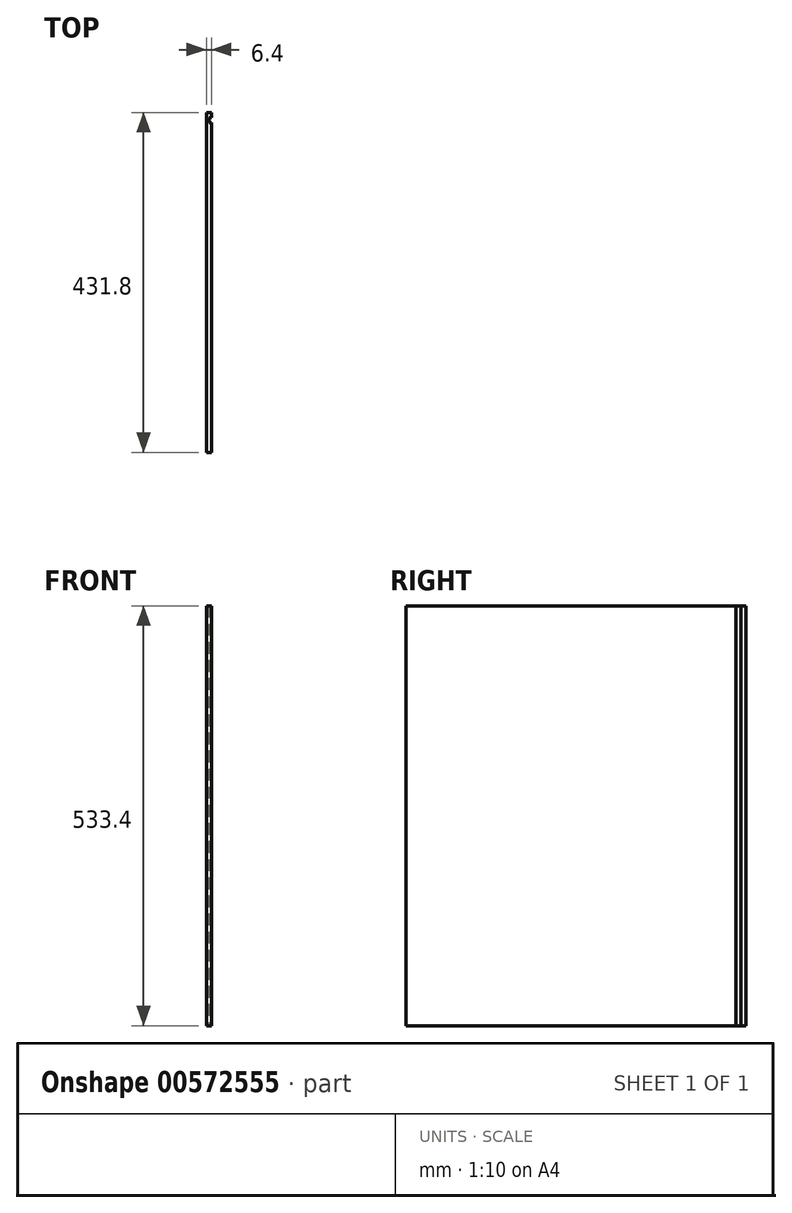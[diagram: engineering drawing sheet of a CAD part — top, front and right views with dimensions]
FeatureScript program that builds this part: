
annotation { "Feature Type Name" : "Feature", "Feature Type Description" : "" }
export const myFeature = defineFeature(function(context is Context, id is Id, definition is map)
    precondition{}
    {
        {
            var Q0;
            Q0=qCreatedBy(makeId("Right.planeOp"),FACE);
            var sketch = newSketch(context, id + "F0", { "sketchPlane" : qUnion([Q0])});
            skLineSegment(sketch, "E0.bottom", {"start": v(-326.3, 269.4) * mm, "end": v(105.5, 269.4) * mm});
            skLineSegment(sketch, "E0.top", {"start": v(-326.3, -264) * mm, "end": v(105.5, -264) * mm});
            skLineSegment(sketch, "E0.left", {"start": v(-326.3, 269.4) * mm, "end": v(-326.3, -264) * mm});
            skLineSegment(sketch, "E0.right", {"start": v(105.5, 269.4) * mm, "end": v(105.5, -264) * mm});
            skLineSegment(sketch, "E1.bottom", {"start": v(99.15, 279.55) * mm, "end": v(92.8, 279.55) * mm});
            skLineSegment(sketch, "E1.top", {"start": v(99.15, -274.17) * mm, "end": v(92.8, -274.17) * mm});
            skLineSegment(sketch, "E1.left", {"start": v(99.15, 279.55) * mm, "end": v(99.15, -274.17) * mm});
            skLineSegment(sketch, "E1.right", {"start": v(92.8, 279.55) * mm, "end": v(92.8, -274.17) * mm});
            skSolve(sketch);
        }
        {
            var Q0;
            {var subQ0=sQuery(id+"F0.wireOp",EDGE,"E0.left");Q0=makeQuery(id+"F0.imprint","IMPRINT",FACE,{"disambiguationData":[TD([[makeQuery(id+"F0.imprint","IMPRINT",EDGE,{"derivedFrom":subQ0}),1.0]])]});}
            var Q1;
            {var subQ0=sQuery(id+"F0.wireOp",EDGE,"E0.right");Q1=makeQuery(id+"F0.imprint","IMPRINT",FACE,{"disambiguationData":[TD([[makeQuery(id+"F0.imprint","IMPRINT",EDGE,{"derivedFrom":subQ0}),-1.0]])]});}
            var Q2;
            {var subQ0=sQuery(id+"F0.wireOp",EDGE,"E1.right");var subQ1=sQuery(id+"F0.wireOp",EDGE,"E0.bottom");var subQ2=makeQuery(id+"F0.imprint","INTERSECT",VERTEX,{"derivedFrom":[subQ1,subQ0]});Q2=makeQuery(id+"F0.imprint","IMPRINT",FACE,{"disambiguationData":[TD([[makeQuery(id+"F0.imprint","IMPRINT",EDGE,{"disambiguationData":[TD([[subQ2,-1.0]])],"derivedFrom":subQ1}),-1.0]])]});}
            extrude(context, id + "F1", {"entities" : qUnion([Q0, Q1, Q2]), "oppositeDirection" : true, "depth" : 3.2 * mm, "offsetDistance" : 25.4 * mm});
        }
        {
            var Q0;
            {var subQ0=sQuery(id+"F0.wireOp",EDGE,"E0.left");Q0=makeQuery(id+"F0.imprint","IMPRINT",FACE,{"disambiguationData":[TD([[makeQuery(id+"F0.imprint","IMPRINT",EDGE,{"derivedFrom":subQ0}),1.0]])]});}
            var Q1;
            {var subQ0=sQuery(id+"F0.wireOp",EDGE,"E0.right");Q1=makeQuery(id+"F0.imprint","IMPRINT",FACE,{"disambiguationData":[TD([[makeQuery(id+"F0.imprint","IMPRINT",EDGE,{"derivedFrom":subQ0}),-1.0]])]});}
            extrude(context, id + "F2", {"entities" : qUnion([Q0, Q1]), "operationType" : NewBodyOperationType.ADD, "depth" : 3.2 * mm, "offsetDistance" : 25.4 * mm});
        }
    });
